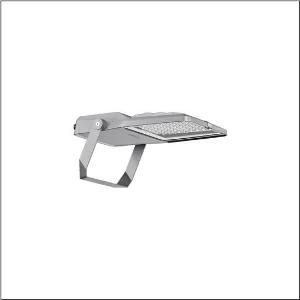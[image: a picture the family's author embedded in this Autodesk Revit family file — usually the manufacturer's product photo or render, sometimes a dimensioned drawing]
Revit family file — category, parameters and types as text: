
# Revit family: floodlight_fl_21_iq_mini___pl52_5xa7771d4d1a_c00e
name_source: partatom
category: Lighting Fixtures
units: mm (PartAtom-declared; Revit-internal decimal feet)

## family parameters
Cut with Voids When Loaded = No
Host = Face
Light Source = No
Part Type = Normal
Room Calculation Point = No
Round Connector Dimension = Use Diameter
Shared = No

## types (1)
- --- (1 x LED, 18610 lm, 143 W, 4000K)
    Apparent Load = 143 VA
    CIE Flux Codes = 26 60 98 100 100
    Color Rendering = 70
    Color Temperature = 4000K
    Default Elevation = 1800 mm
    Description = Floodlight FL 21 iQ mini, floodlight, primary light control with lens, of PMMA, primary optical cover: protective disc, of toughened safety glass, transparent, light distribution: PL52, light emission: direct distribution, installation type: surface-mounted, lamps: LED, High Power LED, rated values: 18.610lm | 143W | 130,1lm/W (begin service life); end service life: 18.610lm | 151,6W; at 50% lumin. flux: 9.305lm | 60,8W | 153lm/W, colour temperature: 4000K, colour rendering: CRI > 70, light colour: 740, light setting 1 begin service life: 100% | 18.610lm | 143W | 130,1lm/W | 4.000K, light setting 1 end service life: 151,6W, further light settings possible, control: Auto-Match, Temp-Guard, Lumen-Switch, Night-Set, Smart-Wire, Light-Fading, Desk-Remote (wireless, voltage-free reading and setting of iQ features in the workshop via application-optimized NFC function/RFID function), optimised constant luminous flux control (CLO 2.0), pre-setting: linear dimming characteristic, with terminal, 6-pole, mains connection: 220..240V, AC, 50/60Hz, luminaire housing, of diecast aluminium, powder-coated, SITECO metallic grey (DB 702S), corrosivity category C5 mid according to DIN EN ISO 12944suitable for swimming poolschlorine-resistant, sealing non-destructively replaceable, mounting bracket, of steel, galvanised, powder-coated, SITECO metallic grey (DB 702S), protection rating (complete): IP66, insulation class (complete): insulation class II (safety insulation), certification: CE, ENEC, VDE, protection symbol: D, impact resistance: IK08, permissible operating ambient temperature: -40..+40°C, permissible operating ambient temperature for outdoor applications: -40..+50°C, standard: DIN EN 12944, LABS conformity tested according to VDMA 24364:2018-05, packaging unit: 1 piece

Light Distribution: PL52
    Height = 70 mm
    Lamp = 1 x LED
    Lamp Light Flux = 18610 lm
    Lamp Power = 143 W
    Lamp count = 1
    Length = 485 mm
    Luminous efficacy = 130 lm/W
    Manufacturer = Siteco
    ModVariant = No
    Model = 5XA7771D4D1A
    Mounting Place = Pole
    Mounting Type = Pole annexe
    Number of Poles = 1
    OnlyDefault = Yes
    Power Factor = 1
    Product Name = Floodlight FL 21 iQ mini | PL52
    Product group = floodlight | pylon annexe
    ProductGroupID = 6201
    Protection Class = Protection class II
    Protection Degree = IP 66
    RLX_Detail_Level = 1
    RLX_Emergency_Light_Flux = 0 lm
    RLX_Emergency_Type = 0
    RLX_Emergency_Type_DB = No
    RlxData = <blob elided: 97201 chars, md5=18687676>
    Socket = socket
    Standby Power = 0 W
    System Light Flux = 18610 lm
    System Power = 143 W
    Type Comments = factory setting: luminous flux: 100 % | dim-lin: 254 | 730 mA
    Type Image = l_1006845.jpg
    URL = http://relux.com
    VarID = @adj_164965
    Voltage = 0 V
    Weight = 0.00 kg
    Width = 337 mm

## geometry (parser evidence)
native form markers: Blend x4, Sweep x13
no freeform markers — native parametric forms only
